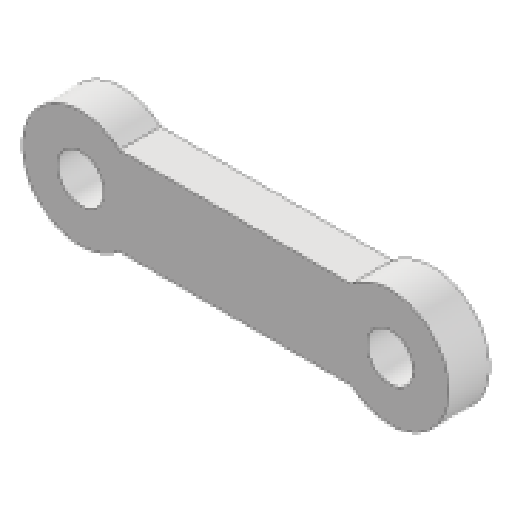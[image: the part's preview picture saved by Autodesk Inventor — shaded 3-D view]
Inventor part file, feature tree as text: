
AUTODESK INVENTOR PART (.ipt)
format: ipt  version: 2025 (Build 290162010, 162A)  size: 99,328 bytes
history: native  units: in
note: dims shown in document units (in); Inventor stores cm internally (conversion verified against a paired STEP export)
features: extrude x1, sketch x1
ambient origin geometry x8: Origin, YZ Plane, XZ Plane, XY Plane, X Axis, Y Axis, Z Axis, Center Point
bodies: Solid1 (feature_tree)
feature tree (2):
  extrude  "Extrusion1"  Depth=0.14in
  sketch  "Sketch1"  dims[d0=0.4in d1=0.16in d2=0.3in d3=0.15in d4=0.4in d5=0.16in d6=1.446in d7=0.14in d8=0.0in]
